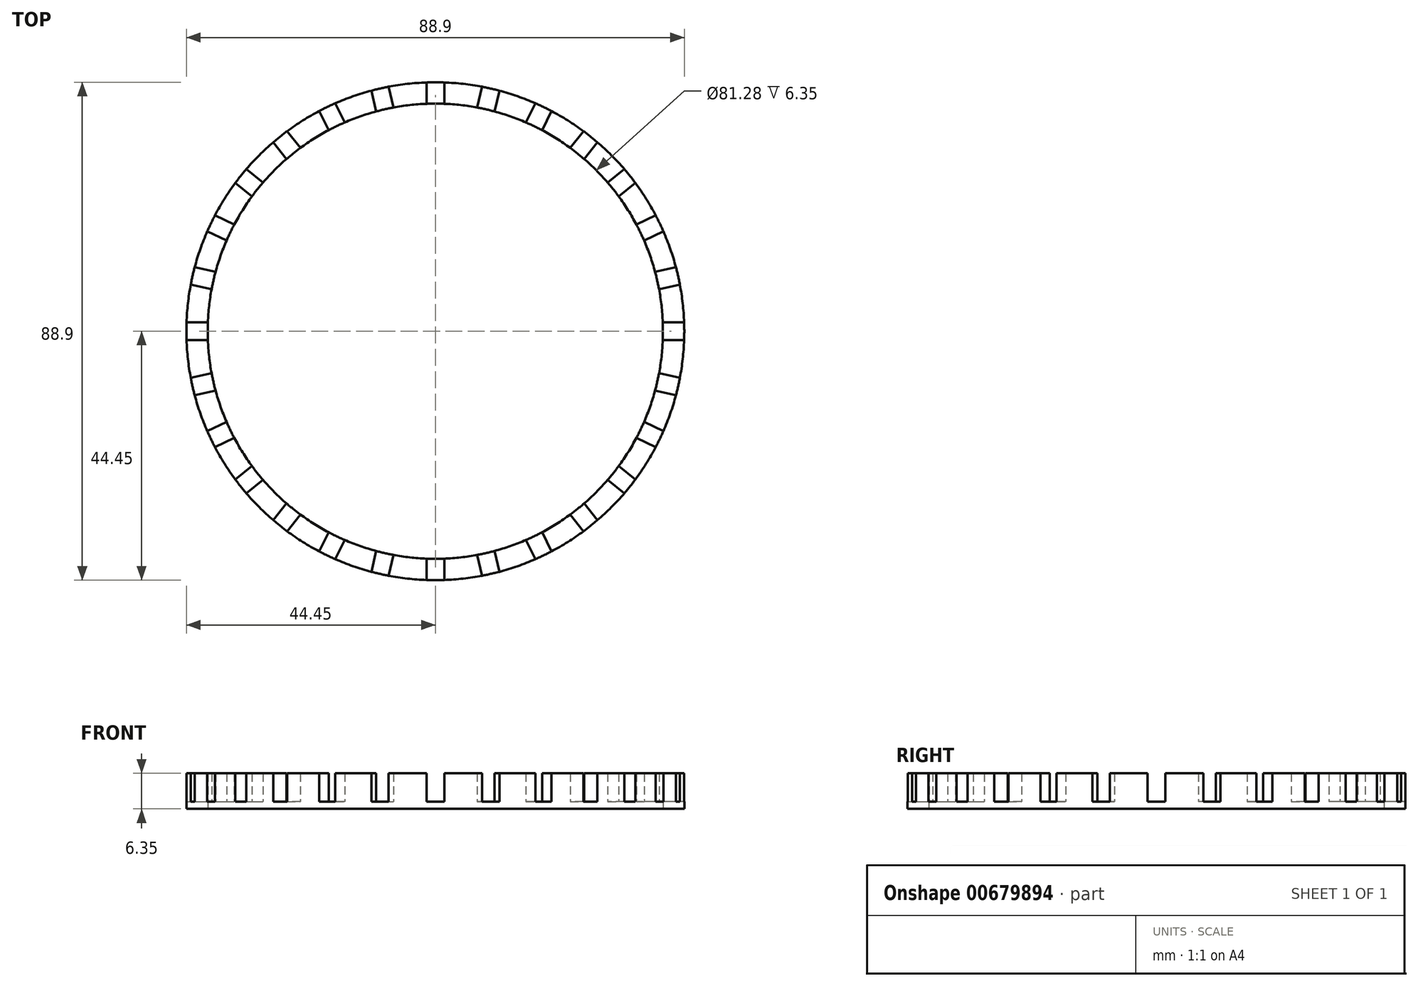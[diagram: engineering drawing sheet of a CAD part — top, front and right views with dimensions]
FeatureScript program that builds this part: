
annotation { "Feature Type Name" : "Feature", "Feature Type Description" : "" }
export const myFeature = defineFeature(function(context is Context, id is Id, definition is map)
    precondition{}
    {
        {
            var Q0;
            Q0=qCreatedBy(makeId("Top.planeOp"),FACE);
            var sketch = newSketch(context, id + "F0", { "sketchPlane" : qUnion([Q0])});
            skCircle(sketch, "E0", {"center": v(0, 0) * mm, "radius": 44.45 * mm});
            skCircle(sketch, "E1", {"center": v(0, 0) * mm, "radius": 40.64 * mm});
            skSolve(sketch);
        }
        {
            var Q0;
            Q0 = qSketchRegion(id + "F0", true);
            extrude(context, id + "F1", {"entities" : qUnion([Q0]), "depth" : 6.35 * mm, "offsetDistance" : 25.4 * mm});
        }
        {
            var Q0;
            Q0=makeQuery(id+"F1.opExtrude","CAP_FACE",FACE,{"disambiguationData":[OSD([sQuery(id+"F0.wireOp",EDGE,"E0"),sQuery(id+"F0.wireOp",EDGE,"E1")])],"isStart":false});
            var sketch = newSketch(context, id + "F2", { "sketchPlane" : qUnion([Q0])});
            skLineSegment(sketch, "E2.bottom", {"start": v(-45.55, 1.59) * mm, "end": v(-38.93, 1.59) * mm});
            skLineSegment(sketch, "E2.top", {"start": v(-45.55, -1.59) * mm, "end": v(-38.93, -1.59) * mm});
            skLineSegment(sketch, "E2.left", {"start": v(-45.55, 1.59) * mm, "end": v(-45.55, -1.59) * mm});
            skLineSegment(sketch, "E2.right", {"start": v(-38.93, 1.59) * mm, "end": v(-38.93, -1.59) * mm});
            skLineSegment(sketch, "E3.1.0", {"start": v(-44.77, 8.59) * mm, "end": v(-38.3, 7.11) * mm});
            skLineSegment(sketch, "E3.1.1", {"start": v(-44.06, 11.68) * mm, "end": v(-37.6, 10.2) * mm});
            skLineSegment(sketch, "E3.1.2", {"start": v(-44.06, 11.68) * mm, "end": v(-44.77, 8.59) * mm});
            skLineSegment(sketch, "E3.1.3", {"start": v(-37.6, 10.2) * mm, "end": v(-38.3, 7.11) * mm});
            skLineSegment(sketch, "E3.2.0", {"start": v(-41.73, 18.34) * mm, "end": v(-35.76, 15.46) * mm});
            skLineSegment(sketch, "E3.2.1", {"start": v(-40.35, 21.2) * mm, "end": v(-34.38, 18.32) * mm});
            skLineSegment(sketch, "E3.2.2", {"start": v(-40.35, 21.2) * mm, "end": v(-41.73, 18.34) * mm});
            skLineSegment(sketch, "E3.2.3", {"start": v(-34.38, 18.32) * mm, "end": v(-35.76, 15.46) * mm});
            skLineSegment(sketch, "E3.3.0", {"start": v(-36.6, 27.16) * mm, "end": v(-31.42, 23.03) * mm});
            skLineSegment(sketch, "E3.3.1", {"start": v(-34.63, 29.64) * mm, "end": v(-29.45, 25.51) * mm});
            skLineSegment(sketch, "E3.3.2", {"start": v(-34.63, 29.64) * mm, "end": v(-36.6, 27.16) * mm});
            skLineSegment(sketch, "E3.3.3", {"start": v(-29.45, 25.51) * mm, "end": v(-31.42, 23.03) * mm});
            skLineSegment(sketch, "E3.4.0", {"start": v(-29.64, 34.63) * mm, "end": v(-25.51, 29.45) * mm});
            skLineSegment(sketch, "E3.4.1", {"start": v(-27.16, 36.6) * mm, "end": v(-23.03, 31.42) * mm});
            skLineSegment(sketch, "E3.4.2", {"start": v(-27.16, 36.6) * mm, "end": v(-29.64, 34.63) * mm});
            skLineSegment(sketch, "E3.4.3", {"start": v(-23.03, 31.42) * mm, "end": v(-25.51, 29.45) * mm});
            skLineSegment(sketch, "E3.5.0", {"start": v(-21.2, 40.35) * mm, "end": v(-18.32, 34.38) * mm});
            skLineSegment(sketch, "E3.5.1", {"start": v(-18.34, 41.73) * mm, "end": v(-15.46, 35.76) * mm});
            skLineSegment(sketch, "E3.5.2", {"start": v(-18.34, 41.73) * mm, "end": v(-21.2, 40.35) * mm});
            skLineSegment(sketch, "E3.5.3", {"start": v(-15.46, 35.76) * mm, "end": v(-18.32, 34.38) * mm});
            skLineSegment(sketch, "E3.6.0", {"start": v(-11.68, 44.06) * mm, "end": v(-10.2, 37.6) * mm});
            skLineSegment(sketch, "E3.6.1", {"start": v(-8.59, 44.77) * mm, "end": v(-7.11, 38.3) * mm});
            skLineSegment(sketch, "E3.6.2", {"start": v(-8.59, 44.77) * mm, "end": v(-11.68, 44.06) * mm});
            skLineSegment(sketch, "E3.6.3", {"start": v(-7.11, 38.3) * mm, "end": v(-10.2, 37.6) * mm});
            skLineSegment(sketch, "E3.7.0", {"start": v(-1.59, 45.55) * mm, "end": v(-1.59, 38.93) * mm});
            skLineSegment(sketch, "E3.7.1", {"start": v(1.59, 45.55) * mm, "end": v(1.59, 38.93) * mm});
            skLineSegment(sketch, "E3.7.2", {"start": v(1.59, 45.55) * mm, "end": v(-1.59, 45.55) * mm});
            skLineSegment(sketch, "E3.7.3", {"start": v(1.59, 38.93) * mm, "end": v(-1.59, 38.93) * mm});
            skLineSegment(sketch, "E3.8.0", {"start": v(8.59, 44.77) * mm, "end": v(7.11, 38.3) * mm});
            skLineSegment(sketch, "E3.8.1", {"start": v(11.68, 44.06) * mm, "end": v(10.2, 37.6) * mm});
            skLineSegment(sketch, "E3.8.2", {"start": v(11.68, 44.06) * mm, "end": v(8.59, 44.77) * mm});
            skLineSegment(sketch, "E3.8.3", {"start": v(10.2, 37.6) * mm, "end": v(7.11, 38.3) * mm});
            skLineSegment(sketch, "E3.9.0", {"start": v(18.34, 41.73) * mm, "end": v(15.46, 35.76) * mm});
            skLineSegment(sketch, "E3.9.1", {"start": v(21.2, 40.35) * mm, "end": v(18.32, 34.38) * mm});
            skLineSegment(sketch, "E3.9.2", {"start": v(21.2, 40.35) * mm, "end": v(18.34, 41.73) * mm});
            skLineSegment(sketch, "E3.9.3", {"start": v(18.32, 34.38) * mm, "end": v(15.46, 35.76) * mm});
            skPoint(sketch, "E3.center", {"position": v(0, 0) * mm});
            skLineSegment(sketch, "E3.anchor1", {"start": v(0, 0) * mm, "end": v(-38.93, -1.59) * mm, "construction": true});
            skLineSegment(sketch, "E3.anchor2", {"start": v(0, 0) * mm, "end": v(38.93, 1.59) * mm, "construction": true});
            skLineSegment(sketch, "E4.2.10.0", {"start": v(27.16, 36.6) * mm, "end": v(23.03, 31.42) * mm});
            skLineSegment(sketch, "E4.3.10.0", {"start": v(29.64, 34.63) * mm, "end": v(25.51, 29.45) * mm});
            skLineSegment(sketch, "E4.6.10.0", {"start": v(29.64, 34.63) * mm, "end": v(27.16, 36.6) * mm});
            skLineSegment(sketch, "E4.9.10.0", {"start": v(25.51, 29.45) * mm, "end": v(23.03, 31.42) * mm});
            skLineSegment(sketch, "E4.2.11.0", {"start": v(34.63, 29.64) * mm, "end": v(29.45, 25.51) * mm});
            skLineSegment(sketch, "E4.3.11.0", {"start": v(36.6, 27.16) * mm, "end": v(31.42, 23.03) * mm});
            skLineSegment(sketch, "E4.6.11.0", {"start": v(36.6, 27.16) * mm, "end": v(34.63, 29.64) * mm});
            skLineSegment(sketch, "E4.9.11.0", {"start": v(31.42, 23.03) * mm, "end": v(29.45, 25.51) * mm});
            skLineSegment(sketch, "E4.2.12.0", {"start": v(40.35, 21.2) * mm, "end": v(34.38, 18.32) * mm});
            skLineSegment(sketch, "E4.3.12.0", {"start": v(41.73, 18.34) * mm, "end": v(35.76, 15.46) * mm});
            skLineSegment(sketch, "E4.6.12.0", {"start": v(41.73, 18.34) * mm, "end": v(40.35, 21.2) * mm});
            skLineSegment(sketch, "E4.9.12.0", {"start": v(35.76, 15.46) * mm, "end": v(34.38, 18.32) * mm});
            skLineSegment(sketch, "E4.2.13.0", {"start": v(44.06, 11.68) * mm, "end": v(37.6, 10.2) * mm});
            skLineSegment(sketch, "E4.3.13.0", {"start": v(44.77, 8.59) * mm, "end": v(38.3, 7.11) * mm});
            skLineSegment(sketch, "E4.6.13.0", {"start": v(44.77, 8.59) * mm, "end": v(44.06, 11.68) * mm});
            skLineSegment(sketch, "E4.9.13.0", {"start": v(38.3, 7.11) * mm, "end": v(37.6, 10.2) * mm});
            skLineSegment(sketch, "E4.2.14.0", {"start": v(45.55, 1.59) * mm, "end": v(38.93, 1.59) * mm});
            skLineSegment(sketch, "E4.3.14.0", {"start": v(45.55, -1.59) * mm, "end": v(38.93, -1.59) * mm});
            skLineSegment(sketch, "E4.6.14.0", {"start": v(45.55, -1.59) * mm, "end": v(45.55, 1.59) * mm});
            skLineSegment(sketch, "E4.9.14.0", {"start": v(38.93, -1.59) * mm, "end": v(38.93, 1.59) * mm});
            skLineSegment(sketch, "E5.MirrorCS", {"start": v(-37.6, -10.2) * mm, "end": v(-38.3, -7.11) * mm});
            skLineSegment(sketch, "E6.MirrorCS", {"start": v(1.59, -38.93) * mm, "end": v(-1.59, -38.93) * mm});
            skLineSegment(sketch, "E7.MirrorCS", {"start": v(18.32, -34.38) * mm, "end": v(15.46, -35.76) * mm});
            skLineSegment(sketch, "E8.MirrorCS", {"start": v(-15.46, -35.76) * mm, "end": v(-18.32, -34.38) * mm});
            skLineSegment(sketch, "E9.MirrorCS", {"start": v(-34.63, -29.64) * mm, "end": v(-36.6, -27.16) * mm});
            skLineSegment(sketch, "E10.MirrorCS", {"start": v(-29.45, -25.51) * mm, "end": v(-31.42, -23.03) * mm});
            skLineSegment(sketch, "E11.MirrorCS", {"start": v(41.73, -18.34) * mm, "end": v(40.35, -21.2) * mm});
            skLineSegment(sketch, "E12.MirrorCS", {"start": v(29.64, -34.63) * mm, "end": v(27.16, -36.6) * mm});
            skLineSegment(sketch, "E13.MirrorCS", {"start": v(36.6, -27.16) * mm, "end": v(34.63, -29.64) * mm});
            skLineSegment(sketch, "E14.MirrorCS", {"start": v(-23.03, -31.42) * mm, "end": v(-25.51, -29.45) * mm});
            skLineSegment(sketch, "E15.MirrorCS", {"start": v(35.76, -15.46) * mm, "end": v(34.38, -18.32) * mm});
            skLineSegment(sketch, "E16.MirrorCS", {"start": v(25.51, -29.45) * mm, "end": v(23.03, -31.42) * mm});
            skLineSegment(sketch, "E17.MirrorCS", {"start": v(38.3, -7.11) * mm, "end": v(37.6, -10.2) * mm});
            skLineSegment(sketch, "E18.MirrorCS", {"start": v(-44.06, -11.68) * mm, "end": v(-44.77, -8.59) * mm});
            skLineSegment(sketch, "E19.MirrorCS", {"start": v(-18.34, -41.73) * mm, "end": v(-21.2, -40.35) * mm});
            skLineSegment(sketch, "E20.MirrorCS", {"start": v(-27.16, -36.6) * mm, "end": v(-29.64, -34.63) * mm});
            skLineSegment(sketch, "E21.MirrorCS", {"start": v(1.59, -45.55) * mm, "end": v(-1.59, -45.55) * mm});
            skLineSegment(sketch, "E22.MirrorCS", {"start": v(-7.11, -38.3) * mm, "end": v(-10.2, -37.6) * mm});
            skLineSegment(sketch, "E23.MirrorCS", {"start": v(-34.38, -18.32) * mm, "end": v(-35.76, -15.46) * mm});
            skLineSegment(sketch, "E24.MirrorCS", {"start": v(-8.59, -44.77) * mm, "end": v(-11.68, -44.06) * mm});
            skLineSegment(sketch, "E25.MirrorCS", {"start": v(21.2, -40.35) * mm, "end": v(18.34, -41.73) * mm});
            skLineSegment(sketch, "E26.MirrorCS", {"start": v(31.42, -23.03) * mm, "end": v(29.45, -25.51) * mm});
            skLineSegment(sketch, "E27.MirrorCS", {"start": v(44.77, -8.59) * mm, "end": v(44.06, -11.68) * mm});
            skLineSegment(sketch, "E28.MirrorCS", {"start": v(-40.35, -21.2) * mm, "end": v(-41.73, -18.34) * mm});
            skLineSegment(sketch, "E29.MirrorCS", {"start": v(11.68, -44.06) * mm, "end": v(8.59, -44.77) * mm});
            skLineSegment(sketch, "E30.MirrorCS", {"start": v(10.2, -37.6) * mm, "end": v(7.11, -38.3) * mm});
            skLineSegment(sketch, "E31.MirrorCS", {"start": v(-41.73, -18.34) * mm, "end": v(-35.76, -15.46) * mm});
            skLineSegment(sketch, "E32.MirrorCS", {"start": v(8.59, -44.77) * mm, "end": v(7.11, -38.3) * mm});
            skLineSegment(sketch, "E33.MirrorCS", {"start": v(-29.64, -34.63) * mm, "end": v(-25.51, -29.45) * mm});
            skLineSegment(sketch, "E34.MirrorCS", {"start": v(44.77, -8.59) * mm, "end": v(38.3, -7.11) * mm});
            skLineSegment(sketch, "E35.MirrorCS", {"start": v(-34.63, -29.64) * mm, "end": v(-29.45, -25.51) * mm});
            skLineSegment(sketch, "E36.MirrorCS", {"start": v(36.6, -27.16) * mm, "end": v(31.42, -23.03) * mm});
            skLineSegment(sketch, "E37.MirrorCS", {"start": v(-18.34, -41.73) * mm, "end": v(-15.46, -35.76) * mm});
            skLineSegment(sketch, "E38.MirrorCS", {"start": v(21.2, -40.35) * mm, "end": v(18.32, -34.38) * mm});
            skLineSegment(sketch, "E39.MirrorCS", {"start": v(-21.2, -40.35) * mm, "end": v(-18.32, -34.38) * mm});
            skLineSegment(sketch, "E40.MirrorCS", {"start": v(-44.77, -8.59) * mm, "end": v(-38.3, -7.11) * mm});
            skLineSegment(sketch, "E41.MirrorCS", {"start": v(18.34, -41.73) * mm, "end": v(15.46, -35.76) * mm});
            skLineSegment(sketch, "E42.MirrorCS", {"start": v(41.73, -18.34) * mm, "end": v(35.76, -15.46) * mm});
            skLineSegment(sketch, "E43.MirrorCS", {"start": v(-44.06, -11.68) * mm, "end": v(-37.6, -10.2) * mm});
            skLineSegment(sketch, "E44.MirrorCS", {"start": v(40.35, -21.2) * mm, "end": v(34.38, -18.32) * mm});
            skLineSegment(sketch, "E45.MirrorCS", {"start": v(44.06, -11.68) * mm, "end": v(37.6, -10.2) * mm});
            skLineSegment(sketch, "E46.MirrorCS", {"start": v(-8.59, -44.77) * mm, "end": v(-7.11, -38.3) * mm});
            skLineSegment(sketch, "E47.MirrorCS", {"start": v(-36.6, -27.16) * mm, "end": v(-31.42, -23.03) * mm});
            skLineSegment(sketch, "E48.MirrorCS", {"start": v(-11.68, -44.06) * mm, "end": v(-10.2, -37.6) * mm});
            skLineSegment(sketch, "E49.MirrorCS", {"start": v(29.64, -34.63) * mm, "end": v(25.51, -29.45) * mm});
            skLineSegment(sketch, "E50.MirrorCS", {"start": v(-40.35, -21.2) * mm, "end": v(-34.38, -18.32) * mm});
            skLineSegment(sketch, "E51.MirrorCS", {"start": v(-1.59, -45.55) * mm, "end": v(-1.59, -38.93) * mm});
            skLineSegment(sketch, "E52.MirrorCS", {"start": v(1.59, -45.55) * mm, "end": v(1.59, -38.93) * mm});
            skLineSegment(sketch, "E53.MirrorCS", {"start": v(27.16, -36.6) * mm, "end": v(23.03, -31.42) * mm});
            skLineSegment(sketch, "E54.MirrorCS", {"start": v(11.68, -44.06) * mm, "end": v(10.2, -37.6) * mm});
            skLineSegment(sketch, "E55.MirrorCS", {"start": v(34.63, -29.64) * mm, "end": v(29.45, -25.51) * mm});
            skLineSegment(sketch, "E56.MirrorCS", {"start": v(-27.16, -36.6) * mm, "end": v(-23.03, -31.42) * mm});
            skSolve(sketch);
        }
        {
            var Q0;
            Q0 = qSketchRegion(id + "F2", true);
            extrude(context, id + "F3", {"entities" : qUnion([Q0]), "operationType" : NewBodyOperationType.REMOVE, "oppositeDirection" : true, "depth" : 5.08 * mm, "offsetDistance" : 25.4 * mm});
        }
    });
